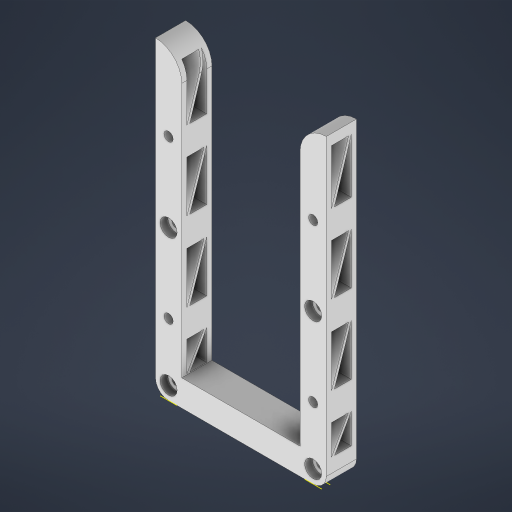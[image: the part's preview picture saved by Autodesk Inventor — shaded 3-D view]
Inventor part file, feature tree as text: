
AUTODESK INVENTOR PART (.ipt)
format: ipt  version: 2023 (Build 270158000, 158)  size: 381,440 bytes
history: native  units: mm
features: reference x6, sketch x5, projected_geometry x5, extrude x4, other x3, plane x2
ambient origin geometry x8: Origin, YZ Plane, XZ Plane, XY Plane, X Axis, Y Axis, Z Axis, Center Point
bodies: Solid1 (feature_tree)
feature tree (25):
  plane  "Work Plane1"
  plane  "Work Plane2"
  extrude  "Extrusion1"  Depth=6.5mm
  extrude  "Spacer Join Countersink"  Depth=60.0mm TaperAngle=360.0deg
  extrude  "nut holes"  Depth=60.0mm TaperAngle=360.0deg
  extrude  "Extrusion4"  Depth=60.0mm TaperAngle=360.0deg
  sketch  "Sketch5"  dims[d30=5.0mm d31=0.0mm d32=4.0mm d33=2.0mm d34=2.0mm d37=2.0mm d38=2.0mm d41=2.0mm d42=2.0mm d43=2.0mm d44=2.0mm d45=2.0mm d47=1.0mm d48=1.0mm d49=1.0mm d50=1.0mm d51=65.0mm d52=0.0mm]
  sketch  "Sketch1"  dims[d0=11.5mm d1=0.0mm d2=6.5mm]
  reference  "Reference1"
  reference  "Reference2"
  sketch  "Sketch2"  dims[d3=3.0mm d4=0.349066mm d5=60.0mm d7=360.0deg]
  sketch  "Sketch3"  dims[d9=6.5mm d18=60.0mm d20=360.0deg]
  reference  "Reference3"
  reference  "Reference4"
  reference  "Reference5"
  reference  "Reference6"
  sketch  "Sketch4"  dims[d22=60.0mm d24=360.0deg d26=60.0mm d28=360.0deg]
  projected_geometry  "Projected Loop2"
  projected_geometry  "Projected Loop3"
  projected_geometry  "Projected Loop4"
  projected_geometry  "Projected Loop5"
  projected_geometry  "Projected Loop6"
  parser-record x1  (decoder bookkeeping rows leaked as tree rows — omitted from the tree; the rows remain in map.json)
  other  "total.iam"
  other  "middle spacer bottom:1"
note: 1 file-system path scrubbed to <path> (originals preserved in map.json)
